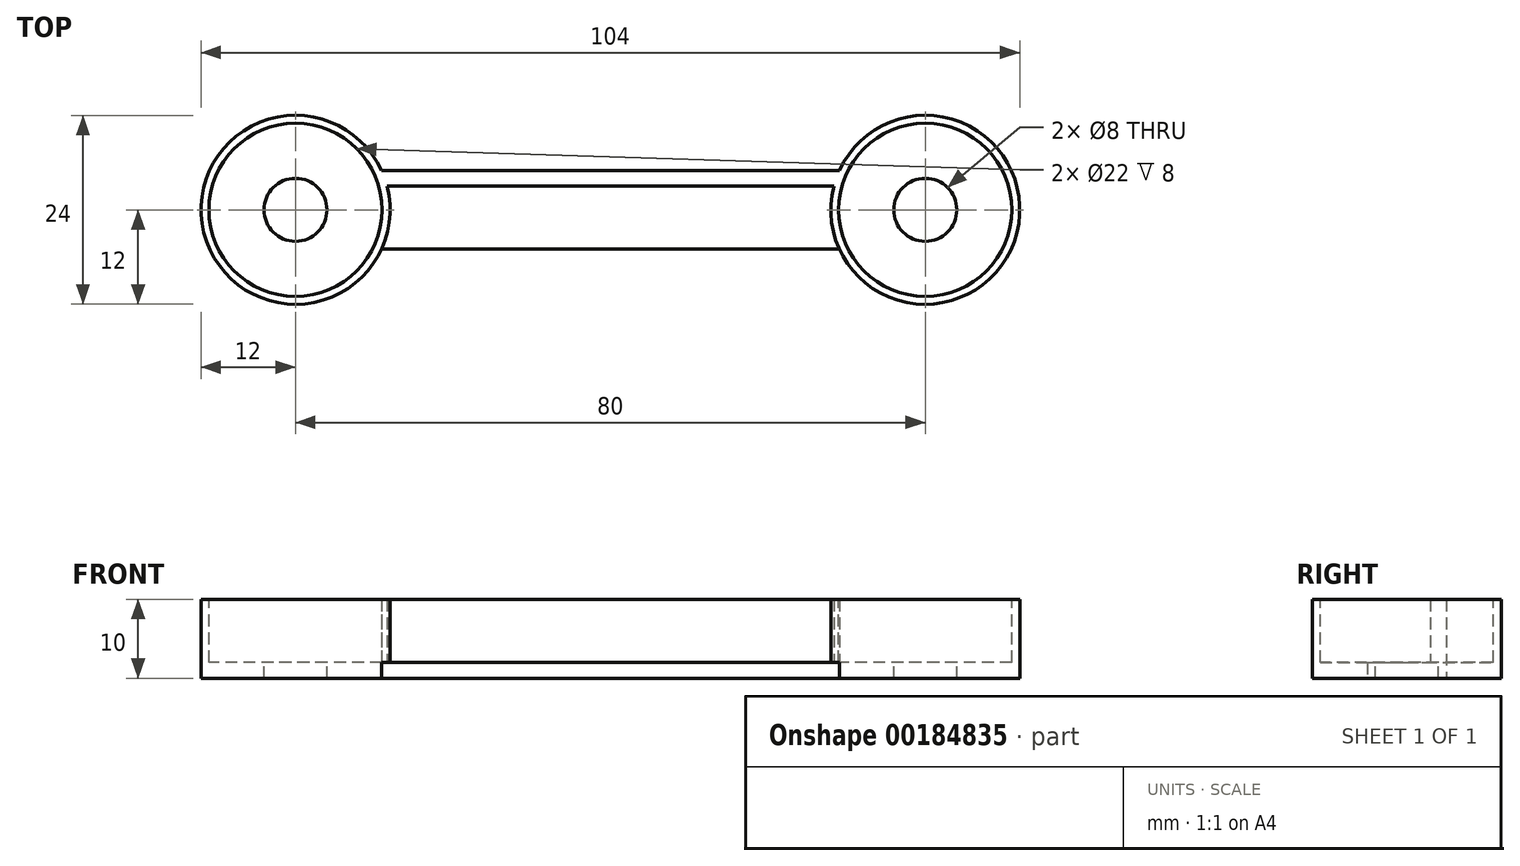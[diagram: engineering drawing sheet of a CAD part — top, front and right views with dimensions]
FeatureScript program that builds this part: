
annotation { "Feature Type Name" : "Feature", "Feature Type Description" : "" }
export const myFeature = defineFeature(function(context is Context, id is Id, definition is map)
    precondition{}
    {
        {
            var Q0;
            Q0=qCreatedBy(makeId("Top.planeOp"),FACE);
            var sketch = newSketch(context, id + "F0", { "sketchPlane" : qUnion([Q0])});
            skLineSegment(sketch, "E0.bottom", {"start": v(0, 0) * mm, "end": v(80, 0) * mm});
            skLineSegment(sketch, "E0.top", {"start": v(0, 10) * mm, "end": v(80, 10) * mm});
            skLineSegment(sketch, "E0.left", {"start": v(0, 0) * mm, "end": v(0, 10) * mm});
            skLineSegment(sketch, "E0.right", {"start": v(80, 0) * mm, "end": v(80, 10) * mm});
            skPoint(sketch, "E1", {"position": v(0, 5) * mm});
            skLineSegment(sketch, "E2", {"start": v(0, 5) * mm, "end": v(116.82, 5) * mm, "construction": true});
            skPoint(sketch, "E3", {"position": v(80, 5) * mm});
            skCircle(sketch, "E4", {"center": v(0, 5) * mm, "radius": 12 * mm});
            skCircle(sketch, "E5", {"center": v(80, 5) * mm, "radius": 12 * mm});
            skSolve(sketch);
        }
        {
            var Q0;
            {var subQ0=sQuery(id+"F0.wireOp",EDGE,"E4");var subQ1=sQuery(id+"F0.wireOp",EDGE,"E0.bottom");var subQ2=makeQuery(id+"F0.imprint","INTERSECT",VERTEX,{"derivedFrom":[subQ1,subQ0]});Q0=makeQuery(id+"F0.imprint","IMPRINT",FACE,{"disambiguationData":[TD([[makeQuery(id+"F0.imprint","IMPRINT",EDGE,{"disambiguationData":[TD([[subQ2,-1.0]])],"derivedFrom":subQ1}),1.0]])]});}
            extrude(context, id + "F1", {"entities" : qUnion([Q0]), "depth" : 2 * mm});
        }
        {
            var Q0;
            {var subQ0=sQuery(id+"F0.wireOp",EDGE,"E0.left");Q0=makeQuery(id+"F0.imprint","IMPRINT",FACE,{"disambiguationData":[TD([[makeQuery(id+"F0.imprint","IMPRINT",EDGE,{"derivedFrom":subQ0}),1.0]])]});}
            var Q1;
            {var subQ0=sQuery(id+"F0.wireOp",EDGE,"E0.right");Q1=makeQuery(id+"F0.imprint","IMPRINT",FACE,{"disambiguationData":[TD([[makeQuery(id+"F0.imprint","IMPRINT",EDGE,{"derivedFrom":subQ0}),1.0]])]});}
            var Q2;
            {var subQ0=sQuery(id+"F0.wireOp",EDGE,"E0.right");Q2=makeQuery(id+"F0.imprint","IMPRINT",FACE,{"disambiguationData":[TD([[makeQuery(id+"F0.imprint","IMPRINT",EDGE,{"derivedFrom":subQ0}),-1.0]])]});}
            var Q3;
            {var subQ0=sQuery(id+"F0.wireOp",EDGE,"E0.left");Q3=makeQuery(id+"F0.imprint","IMPRINT",FACE,{"disambiguationData":[TD([[makeQuery(id+"F0.imprint","IMPRINT",EDGE,{"derivedFrom":subQ0}),-1.0]])]});}
            extrude(context, id + "F2", {"entities" : qUnion([Q0, Q1, Q2, Q3]), "operationType" : NewBodyOperationType.ADD, "depth" : 10 * mm});
        }
        {
            var Q0;
            Q0=makeQuery(id+"F2.opExtrude","CAP_FACE",FACE,{"disambiguationData":[OSD([sQuery(id+"F0.wireOp",EDGE,"E4")])],"isStart":false});
            var sketch = newSketch(context, id + "F3", { "sketchPlane" : qUnion([Q0])});
            skPoint(sketch, "E6", {"position": v(0, 5) * mm});
            skCircle(sketch, "E7", {"center": v(0, 5) * mm, "radius": 4 * mm});
            skCircle(sketch, "E8", {"center": v(0, 5) * mm, "radius": 11 * mm});
            skSolve(sketch);
        }
        {
            var Q0;
            Q0=makeQuery(id+"F3.imprint","IMPRINT",FACE,{"disambiguationData":[TD([[makeQuery(id+"F3.imprint","IMPRINT",EDGE,{"derivedFrom":sQuery(id+"F3.wireOp",EDGE,"E7")}),1.0]])]});
            extrude(context, id + "F4", {"entities" : qUnion([Q0]), "operationType" : NewBodyOperationType.REMOVE, "endBound" : BoundingType.THROUGH_ALL, "oppositeDirection" : true, "depth" : 25 * mm});
        }
        {
            var Q0;
            Q0=makeQuery(id+"F3.imprint","IMPRINT",FACE,{"disambiguationData":[TD([[makeQuery(id+"F3.imprint","IMPRINT",EDGE,{"derivedFrom":sQuery(id+"F3.wireOp",EDGE,"E7")}),-1.0]])]});
            extrude(context, id + "F5", {"entities" : qUnion([Q0]), "operationType" : NewBodyOperationType.REMOVE, "oppositeDirection" : true, "depth" : 8 * mm});
        }
        {
            var Q0;
            Q0=makeQuery(id+"F2.opExtrude","CAP_FACE",FACE,{"disambiguationData":[OSD([sQuery(id+"F0.wireOp",EDGE,"E5")])],"isStart":false});
            var sketch = newSketch(context, id + "F6", { "sketchPlane" : qUnion([Q0])});
            skCircle(sketch, "E9", {"center": v(80, 5) * mm, "radius": 11 * mm});
            skCircle(sketch, "E10", {"center": v(80, 5) * mm, "radius": 4 * mm});
            skSolve(sketch);
        }
        {
            var Q0;
            Q0=makeQuery(id+"F6.imprint","IMPRINT",FACE,{"disambiguationData":[TD([[makeQuery(id+"F6.imprint","IMPRINT",EDGE,{"derivedFrom":sQuery(id+"F6.wireOp",EDGE,"E10")}),1.0]])]});
            extrude(context, id + "F7", {"entities" : qUnion([Q0]), "operationType" : NewBodyOperationType.REMOVE, "endBound" : BoundingType.THROUGH_ALL, "oppositeDirection" : true, "depth" : 25 * mm});
        }
        {
            var Q0;
            Q0=makeQuery(id+"F6.imprint","IMPRINT",FACE,{"disambiguationData":[TD([[makeQuery(id+"F6.imprint","IMPRINT",EDGE,{"derivedFrom":sQuery(id+"F6.wireOp",EDGE,"E9")}),1.0]])]});
            extrude(context, id + "F8", {"entities" : qUnion([Q0]), "operationType" : NewBodyOperationType.REMOVE, "oppositeDirection" : true, "depth" : 8 * mm});
        }
        {
            var Q0;
            Q0=makeQuery(id+"F1.opExtrude","CAP_FACE",FACE,{"disambiguationData":[OSD([sQuery(id+"F0.wireOp",EDGE,"E0.bottom"),sQuery(id+"F0.wireOp",EDGE,"E0.top"),sQuery(id+"F0.wireOp",EDGE,"E4"),sQuery(id+"F0.wireOp",EDGE,"E5")])],"isStart":false});
            var sketch = newSketch(context, id + "F9", { "sketchPlane" : qUnion([Q0])});
            skLineSegment(sketch, "E11.bottom", {"start": v(10.9, 0) * mm, "end": v(80.9, 0) * mm});
            skLineSegment(sketch, "E11.top", {"start": v(10.9, 2) * mm, "end": v(80.9, 2) * mm});
            skLineSegment(sketch, "E11.left", {"start": v(10.9, 0) * mm, "end": v(10.9, 2) * mm});
            skLineSegment(sketch, "E11.right", {"start": v(80.9, 0) * mm, "end": v(80.9, 2) * mm});
            skLineSegment(sketch, "E12", {"start": v(12, 5) * mm, "end": v(68, 5) * mm, "construction": true});
            skLineSegment(sketch, "E13.MirrorCS", {"start": v(10.9, 10) * mm, "end": v(80.9, 10) * mm});
            skLineSegment(sketch, "E14.MirrorCS", {"start": v(10.9, 8) * mm, "end": v(80.9, 8) * mm});
            skSolve(sketch);
        }
        {
            var Q0;
            {var subQ0=sQuery(id+"F9.wireOp",EDGE,"E13.MirrorCS");var subQ1=makeQuery(id+"F1.opExtrude","CAP_EDGE",EDGE,{"disambiguationData":[OSD([sQuery(id+"F0.wireOp",EDGE,"E4")])],"isStart":false});var subQ2=makeQuery(id+"F9.imprint","INTERSECT",VERTEX,{"derivedFrom":[subQ1,subQ0]});Q0=makeQuery(id+"F9.imprint","IMPRINT",FACE,{"disambiguationData":[TD([[makeQuery(id+"F9.imprint","IMPRINT",EDGE,{"disambiguationData":[TD([[subQ2,-1.0]])],"derivedFrom":subQ0}),-1.0]])]});}
            var Q1;
            {var subQ1=makeQuery(id+"F1.opExtrude","CAP_EDGE",EDGE,{"disambiguationData":[OSD([sQuery(id+"F0.wireOp",EDGE,"E4")])],"isStart":false});var subQ5=sQuery(id+"F9.wireOp",EDGE,"E11.top");var subQ7=makeQuery(id+"F9.imprint","INTERSECT",VERTEX,{"derivedFrom":[subQ1,subQ5]});Q1=makeQuery(id+"F9.imprint","IMPRINT",FACE,{"disambiguationData":[TD([[makeQuery(id+"F9.imprint","IMPRINT",EDGE,{"disambiguationData":[TD([[subQ7,-1.0]])],"derivedFrom":subQ5}),-1.0]])]});}
            extrude(context, id + "F10", {"entities" : qUnion([Q0, Q1]), "operationType" : NewBodyOperationType.ADD, "depth" : 8 * mm});
        }
    });
